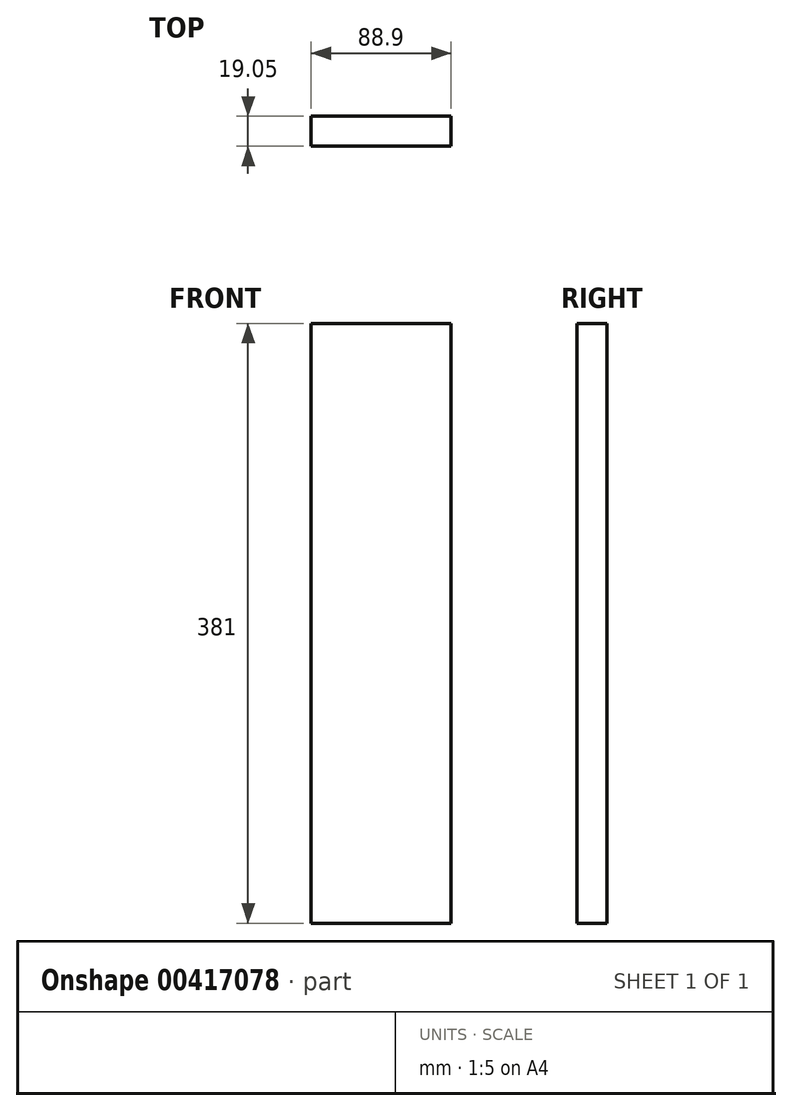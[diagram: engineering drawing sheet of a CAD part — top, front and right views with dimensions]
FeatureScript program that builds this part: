
annotation { "Feature Type Name" : "Feature", "Feature Type Description" : "" }
export const myFeature = defineFeature(function(context is Context, id is Id, definition is map)
    precondition{}
    {
        {
            var Q0;
            Q0=qCreatedBy(makeId("Front.planeOp"),FACE);
            var sketch = newSketch(context, id + "F0", { "sketchPlane" : qUnion([Q0])});
            skLineSegment(sketch, "E0.bottom", {"start": v(0, 0) * mm, "end": v(88.9, 0) * mm});
            skLineSegment(sketch, "E0.top", {"start": v(0, -381) * mm, "end": v(88.9, -381) * mm});
            skLineSegment(sketch, "E0.left", {"start": v(0, 0) * mm, "end": v(0, -381) * mm});
            skLineSegment(sketch, "E0.right", {"start": v(88.9, 0) * mm, "end": v(88.9, -381) * mm});
            skSolve(sketch);
        }
        {
            var Q0;
            Q0 = qSketchRegion(id + "F0", true);
            extrude(context, id + "F1", {"entities" : qUnion([Q0]), "depth" : 19.05 * mm});
        }
    });
